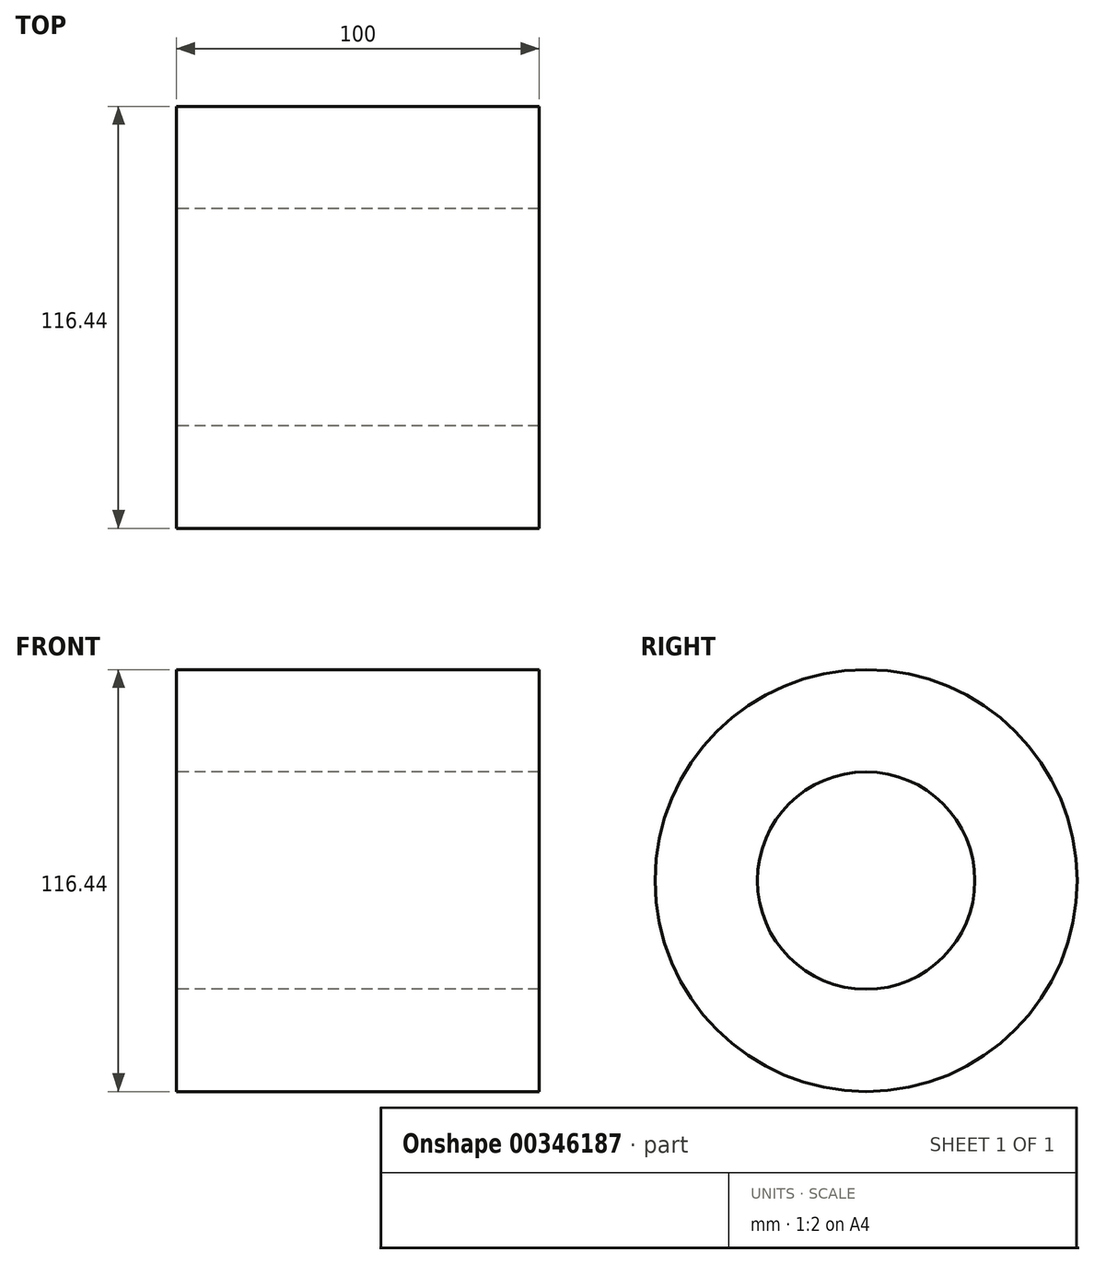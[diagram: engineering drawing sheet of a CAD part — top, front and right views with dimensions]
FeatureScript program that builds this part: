
annotation { "Feature Type Name" : "Feature", "Feature Type Description" : "" }
export const myFeature = defineFeature(function(context is Context, id is Id, definition is map)
    precondition{}
    {
        {
            var Q0;
            Q0=qCreatedBy(makeId("Right.planeOp"),FACE);
            var sketch = newSketch(context, id + "F0", { "sketchPlane" : qUnion([Q0])});
            skCircle(sketch, "E0", {"center": v(0, 0) * mm, "radius": 58.22 * mm});
            skCircle(sketch, "E1", {"center": v(0, 0) * mm, "radius": 30 * mm});
            skSolve(sketch);
        }
        {
            var Q0;
            Q0=makeQuery(id+"F0.imprint","IMPRINT",FACE,{"disambiguationData":[TD([[makeQuery(id+"F0.imprint","IMPRINT",EDGE,{"derivedFrom":sQuery(id+"F0.wireOp",EDGE,"E0")}),1.0]])]});
            extrude(context, id + "F1", {"entities" : qUnion([Q0]), "depth" : 100 * mm});
        }
    });
